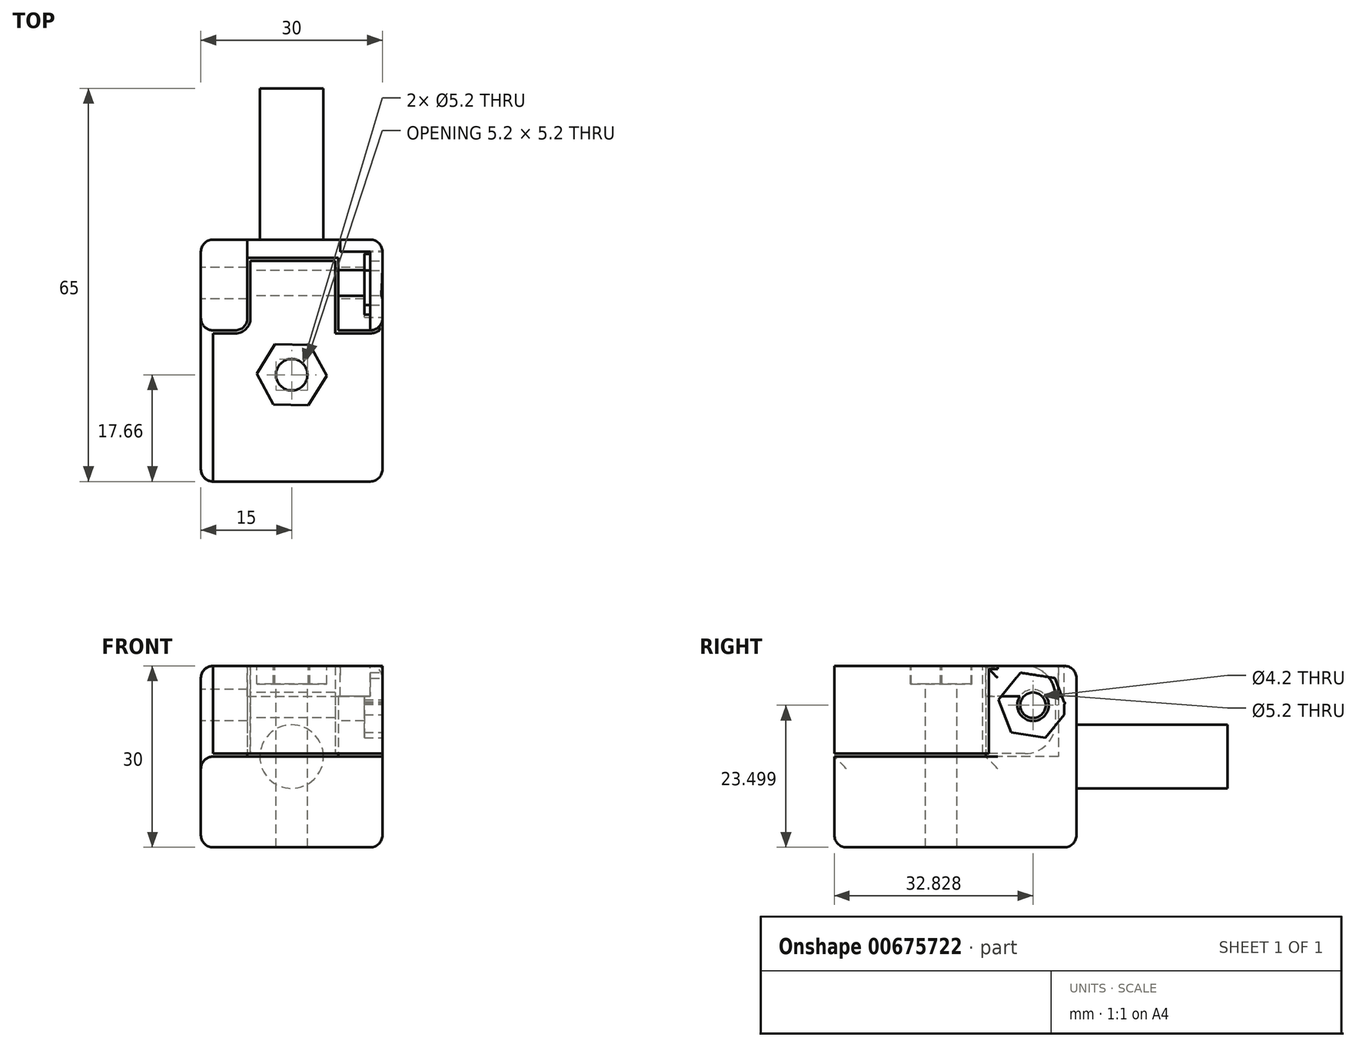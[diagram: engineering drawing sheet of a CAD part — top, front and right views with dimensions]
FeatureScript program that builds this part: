
annotation { "Feature Type Name" : "Feature", "Feature Type Description" : "" }
export const myFeature = defineFeature(function(context is Context, id is Id, definition is map)
    precondition{}
    {
        {
            var Q0;
            Q0=qCreatedBy(makeId("Front.planeOp"),FACE);
            var sketch = newSketch(context, id + "F0", { "sketchPlane" : qUnion([Q0])});
            skLineSegment(sketch, "E0.bottom", {"start": v(-15, -15) * mm, "end": v(15, -15) * mm});
            skLineSegment(sketch, "E0.top", {"start": v(-15, 15) * mm, "end": v(15, 15) * mm});
            skLineSegment(sketch, "E0.left", {"start": v(-15, -15) * mm, "end": v(-15, 15) * mm});
            skLineSegment(sketch, "E0.right", {"start": v(15, -15) * mm, "end": v(15, 15) * mm});
            skPoint(sketch, "E0.middle", {"position": v(0, 0) * mm});
            skSolve(sketch);
        }
        {
            var Q0;
            Q0=makeQuery(id+"F0.imprint","IMPRINT",FACE,{"disambiguationData":[TD([[makeQuery(id+"F0.imprint","IMPRINT",EDGE,{"derivedFrom":sQuery(id+"F0.wireOp",EDGE,"E0.bottom")}),1.0]])]});
            var Q1;
            Q1=qSketchRegion(id+"F0",true);
            extrude(context, id + "F1", {"entities" : qUnion([Q0, Q1]), "depth" : 40 * mm, "offsetDistance" : 25 * mm});
        }
        {
            var Q0;
            Q0=makeQuery(id+"F1.opExtrude","SWEPT_FACE",FACE,{"disambiguationData":[OSD([sQuery(id+"F0.wireOp",EDGE,"E0.left")])]});
            var sketch = newSketch(context, id + "F2", { "sketchPlane" : qUnion([Q0])});
            skLineSegment(sketch, "E1.bottom", {"start": v(15, 15) * mm, "end": v(40, 15) * mm});
            skLineSegment(sketch, "E1.top", {"start": v(15, 0) * mm, "end": v(40, 0) * mm});
            skLineSegment(sketch, "E1.left", {"start": v(15, 15) * mm, "end": v(15, 0) * mm});
            skLineSegment(sketch, "E1.right", {"start": v(40, 15) * mm, "end": v(40, 0) * mm});
            skSolve(sketch);
        }
        {
            var Q0;
            Q0=makeQuery(id+"F2.imprint","IMPRINT",FACE,{"disambiguationData":[TD([[makeQuery(id+"F2.imprint","IMPRINT",EDGE,{"derivedFrom":sQuery(id+"F2.wireOp",EDGE,"E1.bottom")}),1.0]])]});
            extrude(context, id + "F3", {"entities" : qUnion([Q0]), "operationType" : NewBodyOperationType.REMOVE, "endBound" : BoundingType.THROUGH_ALL, "oppositeDirection" : true, "depth" : 25 * mm, "offsetDistance" : 25 * mm});
        }
        {
            var Q0;
            Q0=makeQuery(id+"F3.boolean.opBoolean","COPY",FACE,{"derivedFrom":makeQuery(id+"F3.opExtrude","SWEPT_FACE",FACE,{"disambiguationData":[OSD([sQuery(id+"F2.wireOp",EDGE,"E1.left")])]})});
            var sketch = newSketch(context, id + "F4", { "sketchPlane" : qUnion([Q0])});
            skLineSegment(sketch, "E2.bottom", {"start": v(-7.31, 15) * mm, "end": v(7.69, 15) * mm});
            skLineSegment(sketch, "E2.top", {"start": v(-7.31, 0) * mm, "end": v(7.69, 0) * mm});
            skLineSegment(sketch, "E2.left", {"start": v(-7.31, 15) * mm, "end": v(-7.31, 0) * mm});
            skLineSegment(sketch, "E2.right", {"start": v(7.69, 15) * mm, "end": v(7.69, 0) * mm});
            skSolve(sketch);
        }
        {
            var Q0;
            Q0=makeQuery(id+"F4.imprint","IMPRINT",FACE,{"disambiguationData":[TD([[makeQuery(id+"F4.imprint","IMPRINT",EDGE,{"derivedFrom":sQuery(id+"F4.wireOp",EDGE,"E2.bottom")}),1.0]])]});
            extrude(context, id + "F5", {"entities" : qUnion([Q0]), "operationType" : NewBodyOperationType.REMOVE, "oppositeDirection" : true, "depth" : 12 * mm, "offsetDistance" : 25 * mm});
        }
        {
            var Q0;
            Q0=makeQuery(id+"F1.opExtrude","SWEPT_EDGE",EDGE,{"disambiguationData":[OSD([sQuery(id+"F0.wireOp",EDGE,"E0.top"),sQuery(id+"F0.wireOp",EDGE,"E0.left")])]});
            var Q1;
            Q1=makeQuery(id+"F1.opExtrude","SWEPT_FACE",FACE,{"disambiguationData":[OSD([sQuery(id+"F0.wireOp",EDGE,"E0.left")])]});
            var Q2;
            Q2=makeQuery(id+"F1.opExtrude","CAP_EDGE",EDGE,{"disambiguationData":[OSD([sQuery(id+"F0.wireOp",EDGE,"E0.bottom")])],"isStart":false});
            var Q3;
            Q3=makeQuery(id+"F1.opExtrude","CAP_EDGE",EDGE,{"disambiguationData":[OSD([sQuery(id+"F0.wireOp",EDGE,"E0.right")])],"isStart":false});
            var Q4;
            Q4=makeQuery(id+"F1.opExtrude","SWEPT_EDGE",EDGE,{"disambiguationData":[OSD([sQuery(id+"F0.wireOp",EDGE,"E0.bottom"),sQuery(id+"F0.wireOp",EDGE,"E0.right")])]});
            var Q5;
            Q5=makeQuery(id+"F1.opExtrude","CAP_EDGE",EDGE,{"disambiguationData":[OSD([sQuery(id+"F0.wireOp",EDGE,"E0.right")])],"isStart":true});
            var Q6;
            Q6=makeQuery(id+"F1.opExtrude","SWEPT_EDGE",EDGE,{"disambiguationData":[OSD([sQuery(id+"F0.wireOp",EDGE,"E0.top"),sQuery(id+"F0.wireOp",EDGE,"E0.right")])]});
            var Q7;
            Q7=makeQuery(id+"F3.boolean.opBoolean","INTERSECT",EDGE,{"derivedFrom":[makeQuery(id+"F1.opExtrude","SWEPT_FACE",FACE,{"disambiguationData":[OSD([sQuery(id+"F0.wireOp",EDGE,"E0.right")])]}),makeQuery(id+"F3.opExtrude","SWEPT_FACE",FACE,{"disambiguationData":[OSD([sQuery(id+"F2.wireOp",EDGE,"E1.left")])]})]});
            var Q8;
            Q8=makeQuery(id+"F1.opExtrude","CAP_EDGE",EDGE,{"disambiguationData":[OSD([sQuery(id+"F0.wireOp",EDGE,"E0.top")])],"isStart":true});
            var Q9;
            Q9=makeQuery(id+"F1.opExtrude","CAP_EDGE",EDGE,{"disambiguationData":[OSD([sQuery(id+"F0.wireOp",EDGE,"E0.bottom")])],"isStart":true});
            var Q10;
            Q10=makeQuery(id+"F5.boolean.opBoolean","COPY",EDGE,{"derivedFrom":makeQuery(id+"F5.opExtrude","SWEPT_EDGE",EDGE,{"disambiguationData":[OSD([sQuery(id+"F0.wireOp",EDGE,"E0.top"),sQuery(id+"F0.wireOp",EDGE,"E0.left"),sQuery(id+"F2.wireOp",EDGE,"E1.bottom"),sQuery(id+"F2.wireOp",EDGE,"E1.left"),sQuery(id+"F4.wireOp",EDGE,"E2.bottom"),sQuery(id+"F4.wireOp",EDGE,"E2.left")])]})});
            var Q11;
            Q11=makeQuery(id+"F5.boolean.opBoolean","COPY",EDGE,{"derivedFrom":makeQuery(id+"F5.opExtrude","SWEPT_EDGE",EDGE,{"disambiguationData":[OSD([sQuery(id+"F0.wireOp",EDGE,"E0.top"),sQuery(id+"F0.wireOp",EDGE,"E0.left"),sQuery(id+"F2.wireOp",EDGE,"E1.bottom"),sQuery(id+"F2.wireOp",EDGE,"E1.left"),sQuery(id+"F4.wireOp",EDGE,"E2.bottom"),sQuery(id+"F4.wireOp",EDGE,"E2.right")])]})});
            var Q12;
            Q12=makeQuery(id+"F5.boolean.opBoolean","COPY",EDGE,{"derivedFrom":makeQuery(id+"F5.opExtrude","CAP_EDGE",EDGE,{"disambiguationData":[OSD([sQuery(id+"F4.wireOp",EDGE,"E2.left")])],"isStart":true})});
            var Q13;
            Q13=makeQuery(id+"F5.boolean.opBoolean","COPY",EDGE,{"derivedFrom":makeQuery(id+"F5.opExtrude","CAP_EDGE",EDGE,{"disambiguationData":[OSD([sQuery(id+"F4.wireOp",EDGE,"E2.right")])],"isStart":true})});
            var Q14;
            {var subQ0=sQuery(id+"F0.wireOp",EDGE,"E0.top");var subQ1=sQuery(id+"F0.wireOp",EDGE,"E0.left");var subQ2=sQuery(id+"F2.wireOp",EDGE,"E1.left");Q14=makeQuery(id+"F5.boolean.opBoolean","SPLIT",EDGE,{"disambiguationData":[TD([makeQuery(id+"F1.opExtrude","SWEPT_FACE",FACE,{"disambiguationData":[OSD([subQ1])]})])],"derivedFrom":makeQuery(id+"F3.boolean.opBoolean","COPY",EDGE,{"derivedFrom":makeQuery(id+"F3.opExtrude","SWEPT_EDGE",EDGE,{"disambiguationData":[OSD([subQ0,subQ1,sQuery(id+"F2.wireOp",EDGE,"E1.bottom"),subQ2])]})})});}
            var Q15;
            {var subQ0=sQuery(id+"F0.wireOp",EDGE,"E0.top");var subQ1=sQuery(id+"F2.wireOp",EDGE,"E1.left");Q15=makeQuery(id+"F5.boolean.opBoolean","SPLIT",EDGE,{"disambiguationData":[TD([makeQuery(id+"F1.opExtrude","SWEPT_FACE",FACE,{"disambiguationData":[OSD([sQuery(id+"F0.wireOp",EDGE,"E0.right")])]})])],"derivedFrom":makeQuery(id+"F3.boolean.opBoolean","COPY",EDGE,{"derivedFrom":makeQuery(id+"F3.opExtrude","SWEPT_EDGE",EDGE,{"disambiguationData":[OSD([subQ0,sQuery(id+"F0.wireOp",EDGE,"E0.left"),sQuery(id+"F2.wireOp",EDGE,"E1.bottom"),subQ1])]})})});}
            fillet(context, id + "F6", {"entities" : qUnion([Q0, Q1, Q2, Q3, Q4, Q5, Q6, Q7, Q8, Q9, Q10, Q11, Q12, Q13, Q14, Q15]), "radius" : 2 * mm, "tangentPropagation" : true, "allowEdgeOverflow" : false});
        }
        {
            var Q0;
            Q0=makeQuery(id+"F1.opExtrude","CAP_FACE",FACE,{"disambiguationData":[OSD([sQuery(id+"F0.wireOp",EDGE,"E0.bottom"),sQuery(id+"F0.wireOp",EDGE,"E0.top"),sQuery(id+"F0.wireOp",EDGE,"E0.left"),sQuery(id+"F0.wireOp",EDGE,"E0.right")])],"isStart":true});
            var sketch = newSketch(context, id + "F7", { "sketchPlane" : qUnion([Q0])});
            skCircle(sketch, "E3", {"center": v(0, 0) * mm, "radius": 5.25 * mm});
            skSolve(sketch);
        }
        {
            var Q0;
            Q0=makeQuery(id+"F7.imprint","IMPRINT",FACE,{"disambiguationData":[TD([[makeQuery(id+"F7.imprint","IMPRINT",EDGE,{"derivedFrom":sQuery(id+"F7.wireOp",EDGE,"E3")}),1.0]])]});
            extrude(context, id + "F8", {"entities" : qUnion([Q0]), "operationType" : NewBodyOperationType.ADD, "depth" : 25 * mm, "offsetDistance" : 25 * mm});
        }
        {
            var Q0;
            Q0=makeQuery(id+"F1.opExtrude","SWEPT_FACE",FACE,{"disambiguationData":[OSD([sQuery(id+"F0.wireOp",EDGE,"E0.left")])]});
            var sketch = newSketch(context, id + "F9", { "sketchPlane" : qUnion([Q0])});
            skPoint(sketch, "E4", {"position": v(7.17, 8.5) * mm});
            skSolve(sketch);
        }
        {
            var Q0;
            Q0=sQuery(id+"F9.wireOp",VERTEX,"E4");
            var Q1;
            Q1=makeQuery(id+"F1.opExtrude","SWEPT_BODY",BODY,{"disambiguationData":[OSD([sQuery(id+"F0.wireOp",EDGE,"E0.bottom"),sQuery(id+"F0.wireOp",EDGE,"E0.top"),sQuery(id+"F0.wireOp",EDGE,"E0.left"),sQuery(id+"F0.wireOp",EDGE,"E0.right")])]});
            hole(context, id + "F10", {"style" : HoleStyle.SIMPLE, "endStyle" : HoleEndStyle.BLIND, "holeDiameter" : 5.2 * mm, "majorDiameter" : 5 * mm, "holeDepth" : 60 * mm, "isTappedThrough" : true, "tappedDepth" : 12.7 * mm, "tapClearance" : 3, "locations" : qUnion([Q0]), "scope" : qUnion([Q1])});
        }
        {
            var Q0;
            Q0=makeQuery(id+"F5.boolean.opBoolean","MERGE",FACE,{"derivedFrom":[makeQuery(id+"F3.boolean.opBoolean","COPY",FACE,{"derivedFrom":makeQuery(id+"F3.opExtrude","SWEPT_FACE",FACE,{"disambiguationData":[OSD([sQuery(id+"F2.wireOp",EDGE,"E1.top")])]})}),makeQuery(id+"F5.opExtrude","SWEPT_FACE",FACE,{"disambiguationData":[OSD([sQuery(id+"F4.wireOp",EDGE,"E2.top")])]})]});
            var sketch = newSketch(context, id + "F11", { "sketchPlane" : qUnion([Q0])});
            skLineSegment(sketch, "E5.0", {"start": v(13, -40) * mm, "end": v(-13, -40) * mm});
            skLineSegment(sketch, "E6.0.0", {"start": v(-9.31, -15) * mm, "end": v(-13, -15) * mm});
            skLineSegment(sketch, "E6.0.1", {"start": v(-13, -15) * mm, "end": v(-13, -40) * mm});
            skLineSegment(sketch, "E6.0.2", {"start": v(-13, -40) * mm, "end": v(13, -40) * mm});
            skArc(sketch, "E6.0.3", {"start": v(13, -40) * mm, "mid": v(14.41, -39.41) * mm, "end": v(15, -38) * mm});
            skLineSegment(sketch, "E6.0.4", {"start": v(15, -38) * mm, "end": v(15, -13) * mm});
            skArc(sketch, "E6.0.5", {"start": v(15, -13) * mm, "mid": v(14.41, -14.41) * mm, "end": v(13, -15) * mm});
            skLineSegment(sketch, "E6.0.6", {"start": v(13, -15) * mm, "end": v(9.69, -15) * mm});
            skArc(sketch, "E6.0.7", {"start": v(9.69, -15) * mm, "mid": v(8.27, -14.41) * mm, "end": v(7.69, -13) * mm});
            skLineSegment(sketch, "E6.0.8", {"start": v(7.69, -13) * mm, "end": v(7.69, -3) * mm});
            skLineSegment(sketch, "E6.0.9", {"start": v(7.69, -3) * mm, "end": v(-7.31, -3) * mm});
            skLineSegment(sketch, "E6.0.10", {"start": v(-7.31, -3) * mm, "end": v(-7.31, -13) * mm});
            skArc(sketch, "E6.0.11", {"start": v(-7.31, -13) * mm, "mid": v(-7.9, -14.41) * mm, "end": v(-9.31, -15) * mm});
            skSolve(sketch);
        }
        {
            var Q0;
            Q0=qSketchRegion(id+"F11",true);
            var Q1;
            Q1=makeQuery(id+"F1.opExtrude","SWEPT_FACE",FACE,{"disambiguationData":[OSD([sQuery(id+"F0.wireOp",EDGE,"E0.top")])]});
            extrude(context, id + "F12", {"entities" : qUnion([Q0]), "endBound" : BoundingType.UP_TO_SURFACE, "depth" : 25 * mm, "endBoundEntityFace" : qUnion([Q1]), "offsetDistance" : 25 * mm});
        }
        {
            var Q0;
            Q0=makeQuery(id+"F1.opExtrude","SWEPT_BODY",BODY,{"disambiguationData":[OSD([sQuery(id+"F0.wireOp",EDGE,"E0.bottom"),sQuery(id+"F0.wireOp",EDGE,"E0.top"),sQuery(id+"F0.wireOp",EDGE,"E0.left"),sQuery(id+"F0.wireOp",EDGE,"E0.right")])]});
            var Q1;
            Q1=makeQuery(id+"F12.opExtrude","SWEPT_BODY",BODY,{"disambiguationData":[OSD([sQuery(id+"F11.wireOp",EDGE,"E6.0.0"),sQuery(id+"F11.wireOp",EDGE,"E6.0.1"),sQuery(id+"F11.wireOp",EDGE,"E6.0.2"),sQuery(id+"F11.wireOp",EDGE,"E6.0.3"),sQuery(id+"F11.wireOp",EDGE,"E6.0.4"),sQuery(id+"F11.wireOp",EDGE,"E6.0.5"),sQuery(id+"F11.wireOp",EDGE,"E6.0.6"),sQuery(id+"F11.wireOp",EDGE,"E6.0.7"),sQuery(id+"F11.wireOp",EDGE,"E6.0.8"),sQuery(id+"F11.wireOp",EDGE,"E6.0.9"),sQuery(id+"F11.wireOp",EDGE,"E6.0.10"),sQuery(id+"F11.wireOp",EDGE,"E6.0.11")])]});
            booleanBodies(context, id + "F13", {"operationType" : BooleanOperationType.SUBTRACTION, "tools" : qUnion([Q0]), "targets" : qUnion([Q1]), "offset" : true, "offsetAll" : true, "offsetDistance" : .5 * mm, "keepTools" : true});
        }
        {
            var Q0;
            Q0=makeQuery(id+"F13.tempBoolean.opBoolean","SPLIT",FACE,{"disambiguationData":[TD([makeQuery(id+"F13.offsetTempBody.opPattern","COPY",FACE,{"derivedFrom":makeQuery(id+"F10.hole-0.boolean.opBoolean","COPY",FACE,{"disambiguationData":[TD([makeQuery(id+"F1.opExtrude","SWEPT_FACE",FACE,{"disambiguationData":[OSD([sQuery(id+"F0.wireOp",EDGE,"E0.left")])]})])],"derivedFrom":makeQuery(id+"F10.hole-0.opRevolve","SWEPT_FACE",FACE,{"disambiguationData":[OSD([sQuery(id+"F10.hole-0.sketch.wireOp",EDGE,"core_line_2")])]})}),"instanceName":"1"})])],"derivedFrom":makeQuery(id+"F12.opExtrude","SWEPT_FACE",FACE,{"disambiguationData":[OSD([sQuery(id+"F11.wireOp",EDGE,"E6.0.10")])]})});
            extrude(context, id + "F14", {"entities" : qUnion([Q0]), "operationType" : NewBodyOperationType.REMOVE, "endBound" : BoundingType.THROUGH_ALL, "oppositeDirection" : true, "depth" : 25 * mm, "offsetDistance" : 25 * mm});
        }
        {
            var Q0;
            Q0=makeQuery(id+"F1.opExtrude","SWEPT_FACE",FACE,{"disambiguationData":[OSD([sQuery(id+"F0.wireOp",EDGE,"E0.top")])]});
            var sketch = newSketch(context, id + "F15", { "sketchPlane" : qUnion([Q0])});
            skLineSegment(sketch, "E7.bottom", {"start": v(-7.36, 0) * mm, "end": v(8.03, 0) * mm});
            skLineSegment(sketch, "E7.top", {"start": v(-7.36, -3) * mm, "end": v(8.03, -3) * mm});
            skLineSegment(sketch, "E7.left", {"start": v(-7.36, 0) * mm, "end": v(-7.36, -3) * mm});
            skLineSegment(sketch, "E7.right", {"start": v(8.03, 0) * mm, "end": v(8.03, -3) * mm});
            skSolve(sketch);
        }
        {
            var Q0;
            {var subQ0=sQuery(id+"F15.wireOp",EDGE,"E7.bottom");Q0=makeQuery(id+"F15.imprint","IMPRINT",FACE,{"disambiguationData":[TD([[makeQuery(id+"F15.imprint","IMPRINT",EDGE,{"derivedFrom":subQ0}),-1.0]])]});}
            var Q1;
            {var subQ0=sQuery(id+"F15.wireOp",EDGE,"E7.top");Q1=makeQuery(id+"F15.imprint","IMPRINT",FACE,{"disambiguationData":[TD([[makeQuery(id+"F15.imprint","IMPRINT",EDGE,{"derivedFrom":subQ0}),-1.0]])]});}
            extrude(context, id + "F16", {"entities" : qUnion([Q0, Q1]), "operationType" : NewBodyOperationType.REMOVE, "oppositeDirection" : true, "depth" : 5 * mm, "offsetDistance" : 25 * mm});
        }
        {
            var Q0;
            Q0=makeQuery(id+"F12.opExtrude","CAP_FACE",FACE,{"disambiguationData":[OSD([sQuery(id+"F11.wireOp",EDGE,"E6.0.0"),sQuery(id+"F11.wireOp",EDGE,"E6.0.1"),sQuery(id+"F11.wireOp",EDGE,"E6.0.2"),sQuery(id+"F11.wireOp",EDGE,"E6.0.3"),sQuery(id+"F11.wireOp",EDGE,"E6.0.4"),sQuery(id+"F11.wireOp",EDGE,"E6.0.5"),sQuery(id+"F11.wireOp",EDGE,"E6.0.6"),sQuery(id+"F11.wireOp",EDGE,"E6.0.7"),sQuery(id+"F11.wireOp",EDGE,"E6.0.8"),sQuery(id+"F11.wireOp",EDGE,"E6.0.9"),sQuery(id+"F11.wireOp",EDGE,"E6.0.10"),sQuery(id+"F11.wireOp",EDGE,"E6.0.11")])],"isStart":false});
            var sketch = newSketch(context, id + "F17", { "sketchPlane" : qUnion([Q0])});
            skPoint(sketch, "E8", {"position": v(0, -22.34) * mm});
            skSolve(sketch);
        }
        {
            var Q0;
            Q0=sQuery(id+"F17.wireOp",VERTEX,"E8");
            var Q1;
            Q1=makeQuery(id+"F1.opExtrude","SWEPT_BODY",BODY,{"disambiguationData":[OSD([sQuery(id+"F0.wireOp",EDGE,"E0.bottom"),sQuery(id+"F0.wireOp",EDGE,"E0.top"),sQuery(id+"F0.wireOp",EDGE,"E0.left"),sQuery(id+"F0.wireOp",EDGE,"E0.right")])]});
            var Q2;
            Q2=makeQuery(id+"F12.opExtrude","SWEPT_BODY",BODY,{"disambiguationData":[OSD([sQuery(id+"F11.wireOp",EDGE,"E6.0.0"),sQuery(id+"F11.wireOp",EDGE,"E6.0.1"),sQuery(id+"F11.wireOp",EDGE,"E6.0.2"),sQuery(id+"F11.wireOp",EDGE,"E6.0.3"),sQuery(id+"F11.wireOp",EDGE,"E6.0.4"),sQuery(id+"F11.wireOp",EDGE,"E6.0.5"),sQuery(id+"F11.wireOp",EDGE,"E6.0.6"),sQuery(id+"F11.wireOp",EDGE,"E6.0.7"),sQuery(id+"F11.wireOp",EDGE,"E6.0.8"),sQuery(id+"F11.wireOp",EDGE,"E6.0.9"),sQuery(id+"F11.wireOp",EDGE,"E6.0.10"),sQuery(id+"F11.wireOp",EDGE,"E6.0.11")])]});
            hole(context, id + "F18", {"style" : HoleStyle.SIMPLE, "endStyle" : HoleEndStyle.THROUGH, "holeDiameter" : 5.2 * mm, "majorDiameter" : 4.83 * mm, "isTappedThrough" : true, "tappedDepth" : 12.7 * mm, "tapClearance" : 3, "locations" : qUnion([Q0]), "scope" : qUnion([Q1, Q2])});
        }
        {
            var Q0;
            Q0=makeQuery(id+"F1.opExtrude","SWEPT_FACE",FACE,{"disambiguationData":[OSD([sQuery(id+"F0.wireOp",EDGE,"E0.right")])]});
            var sketch = newSketch(context, id + "F19", { "sketchPlane" : qUnion([Q0])});
            skCircle(sketch, "E9.cCircle", {"center": v(-7.17, 8.5) * mm, "radius": 4.6 * mm, "construction": true});
            skPoint(sketch, "E9.cCircle.perimeterSnap0", {"position": v(-13, 6.5) * mm});
            skLineSegment(sketch, "E9.0", {"start": v(-1.88, 8.9) * mm, "end": v(-4.18, 4.1) * mm});
            skLineSegment(sketch, "E9.1", {"start": v(-4.18, 4.1) * mm, "end": v(-9.48, 3.72) * mm});
            skLineSegment(sketch, "E9.2", {"start": v(-9.48, 3.72) * mm, "end": v(-12.47, 8.1) * mm});
            skLineSegment(sketch, "E9.3", {"start": v(-12.47, 8.1) * mm, "end": v(-10.16, 12.9) * mm});
            skLineSegment(sketch, "E9.4", {"start": v(-10.16, 12.9) * mm, "end": v(-4.86, 13.28) * mm});
            skLineSegment(sketch, "E9.5", {"start": v(-4.86, 13.28) * mm, "end": v(-1.88, 8.9) * mm});
            skPoint(sketch, "E9.0.midPoint", {"position": v(-3.03, 6.5) * mm});
            skPoint(sketch, "E9.0.midPoint.positionSnap0", {"position": v(-13, 6.5) * mm});
            skSolve(sketch);
        }
        {
            var Q0;
            Q0=makeQuery(id+"F19.imprint","IMPRINT",FACE,{"disambiguationData":[TD([[makeQuery(id+"F19.imprint","IMPRINT",EDGE,{"derivedFrom":sQuery(id+"F19.wireOp",EDGE,"E9.0")}),-1.0]])]});
            extrude(context, id + "F20", {"entities" : qUnion([Q0]), "operationType" : NewBodyOperationType.REMOVE, "oppositeDirection" : true, "depth" : 3 * mm, "offsetDistance" : 25 * mm});
        }
        {
            var Q0;
            Q0=makeQuery(id+"F13.tempBoolean.opBoolean","COPY",EDGE,{"derivedFrom":makeQuery(id+"F13.offsetTempBody.opPattern","COPY",EDGE,{"derivedFrom":makeQuery(id+"F5.boolean.opBoolean","COPY",EDGE,{"derivedFrom":makeQuery(id+"F5.opExtrude","CAP_EDGE",EDGE,{"disambiguationData":[OSD([sQuery(id+"F4.wireOp",EDGE,"E2.top")])],"isStart":false})}),"instanceName":"1"})});
            var Q1;
            Q1=makeQuery(id+"F13.tempBoolean.opBoolean","INTERSECT",EDGE,{"derivedFrom":[makeQuery(id+"F12.opExtrude","CAP_FACE",FACE,{"disambiguationData":[OSD([sQuery(id+"F11.wireOp",EDGE,"E6.0.0"),sQuery(id+"F11.wireOp",EDGE,"E6.0.1"),sQuery(id+"F11.wireOp",EDGE,"E6.0.2"),sQuery(id+"F11.wireOp",EDGE,"E6.0.3"),sQuery(id+"F11.wireOp",EDGE,"E6.0.4"),sQuery(id+"F11.wireOp",EDGE,"E6.0.5"),sQuery(id+"F11.wireOp",EDGE,"E6.0.6"),sQuery(id+"F11.wireOp",EDGE,"E6.0.7"),sQuery(id+"F11.wireOp",EDGE,"E6.0.8"),sQuery(id+"F11.wireOp",EDGE,"E6.0.9"),sQuery(id+"F11.wireOp",EDGE,"E6.0.10"),sQuery(id+"F11.wireOp",EDGE,"E6.0.11")])],"isStart":false}),makeQuery(id+"F13.offsetTempBody.opPattern","COPY",FACE,{"derivedFrom":makeQuery(id+"F5.boolean.opBoolean","COPY",FACE,{"derivedFrom":makeQuery(id+"F5.opExtrude","CAP_FACE",FACE,{"disambiguationData":[OSD([sQuery(id+"F4.wireOp",EDGE,"E2.bottom"),sQuery(id+"F4.wireOp",EDGE,"E2.top"),sQuery(id+"F4.wireOp",EDGE,"E2.left"),sQuery(id+"F4.wireOp",EDGE,"E2.right")])],"isStart":false})}),"instanceName":"1"})]});
            fillet(context, id + "F21", {"entities" : qUnion([Q0, Q1]), "radius" : 5 * mm, "tangentPropagation" : true, "allowEdgeOverflow" : false});
        }
        {
            var Q0;
            Q0=makeQuery(id+"F12.opExtrude","CAP_FACE",FACE,{"disambiguationData":[OSD([sQuery(id+"F11.wireOp",EDGE,"E6.0.0"),sQuery(id+"F11.wireOp",EDGE,"E6.0.1"),sQuery(id+"F11.wireOp",EDGE,"E6.0.2"),sQuery(id+"F11.wireOp",EDGE,"E6.0.3"),sQuery(id+"F11.wireOp",EDGE,"E6.0.4"),sQuery(id+"F11.wireOp",EDGE,"E6.0.5"),sQuery(id+"F11.wireOp",EDGE,"E6.0.6"),sQuery(id+"F11.wireOp",EDGE,"E6.0.7"),sQuery(id+"F11.wireOp",EDGE,"E6.0.8"),sQuery(id+"F11.wireOp",EDGE,"E6.0.9"),sQuery(id+"F11.wireOp",EDGE,"E6.0.10"),sQuery(id+"F11.wireOp",EDGE,"E6.0.11")])],"isStart":false});
            var sketch = newSketch(context, id + "F22", { "sketchPlane" : qUnion([Q0])});
            skCircle(sketch, "E10.cCircle", {"center": v(0, -22.34) * mm, "radius": 5 * mm, "construction": true});
            skLineSegment(sketch, "E10.0", {"start": v(5.77, -22.48) * mm, "end": v(2.76, -27.4) * mm});
            skLineSegment(sketch, "E10.1", {"start": v(2.76, -27.4) * mm, "end": v(-3, -27.27) * mm});
            skLineSegment(sketch, "E10.2", {"start": v(-3, -27.27) * mm, "end": v(-5.77, -22.2) * mm});
            skLineSegment(sketch, "E10.3", {"start": v(-5.77, -22.2) * mm, "end": v(-2.76, -17.27) * mm});
            skLineSegment(sketch, "E10.4", {"start": v(-2.76, -17.27) * mm, "end": v(3, -17.41) * mm});
            skLineSegment(sketch, "E10.5", {"start": v(3, -17.41) * mm, "end": v(5.77, -22.48) * mm});
            skPoint(sketch, "E10.0.midPoint", {"position": v(4.27, -24.94) * mm});
            skSolve(sketch);
        }
        {
            var Q0;
            Q0=makeQuery(id+"F22.imprint","IMPRINT",FACE,{"disambiguationData":[TD([[makeQuery(id+"F22.imprint","IMPRINT",EDGE,{"derivedFrom":sQuery(id+"F22.wireOp",EDGE,"E10.0")}),-1.0]])]});
            extrude(context, id + "F23", {"entities" : qUnion([Q0]), "operationType" : NewBodyOperationType.REMOVE, "oppositeDirection" : true, "depth" : 3 * mm, "offsetDistance" : 25 * mm});
        }
        {
            var Q0;
            Q0=makeQuery(id+"F1.opExtrude","SWEPT_FACE",FACE,{"disambiguationData":[OSD([sQuery(id+"F0.wireOp",EDGE,"E0.right")])]});
            var sketch = newSketch(context, id + "F24", { "sketchPlane" : qUnion([Q0])});
            skCircle(sketch, "E11.cCircle", {"center": v(-7.17, 8.5) * mm, "radius": 5 * mm, "construction": true});
            skLineSegment(sketch, "E11.0", {"start": v(-1.47, 7.6) * mm, "end": v(-5.1, 3.1) * mm});
            skLineSegment(sketch, "E11.1", {"start": v(-5.1, 3.1) * mm, "end": v(-10.8, 4.01) * mm});
            skLineSegment(sketch, "E11.2", {"start": v(-10.8, 4.01) * mm, "end": v(-12.87, 9.4) * mm});
            skLineSegment(sketch, "E11.3", {"start": v(-12.87, 9.4) * mm, "end": v(-9.24, 13.89) * mm});
            skLineSegment(sketch, "E11.4", {"start": v(-9.24, 13.89) * mm, "end": v(-3.54, 12.99) * mm});
            skLineSegment(sketch, "E11.5", {"start": v(-3.54, 12.99) * mm, "end": v(-1.47, 7.6) * mm});
            skPoint(sketch, "E11.0.midPoint", {"position": v(-3.29, 5.35) * mm});
            skSolve(sketch);
        }
        {
            var Q0;
            {var subQ7=sQuery(id+"F24.wireOp",EDGE,"E11.1");Q0=makeQuery(id+"F24.imprint","IMPRINT",FACE,{"disambiguationData":[TD([[makeQuery(id+"F24.imprint","IMPRINT",EDGE,{"derivedFrom":subQ7}),-1.0]])]});}
            var Q1;
            {var subQ0=sQuery(id+"F24.wireOp",EDGE,"E11.4");var subQ1=sQuery(id+"F24.wireOp",EDGE,"E11.3");var subQ2=makeQuery(id+"F24.imprint","INTERSECT",VERTEX,{"derivedFrom":[subQ1,subQ0]});Q1=makeQuery(id+"F24.imprint","IMPRINT",FACE,{"disambiguationData":[TD([[makeQuery(id+"F24.imprint","IMPRINT",EDGE,{"disambiguationData":[TD([[subQ2,1.0]])],"derivedFrom":subQ1}),-1.0]])]});}
            extrude(context, id + "F25", {"entities" : qUnion([Q0, Q1]), "operationType" : NewBodyOperationType.REMOVE, "oppositeDirection" : true, "depth" : 3 * mm, "offsetDistance" : 25 * mm});
        }
    });
